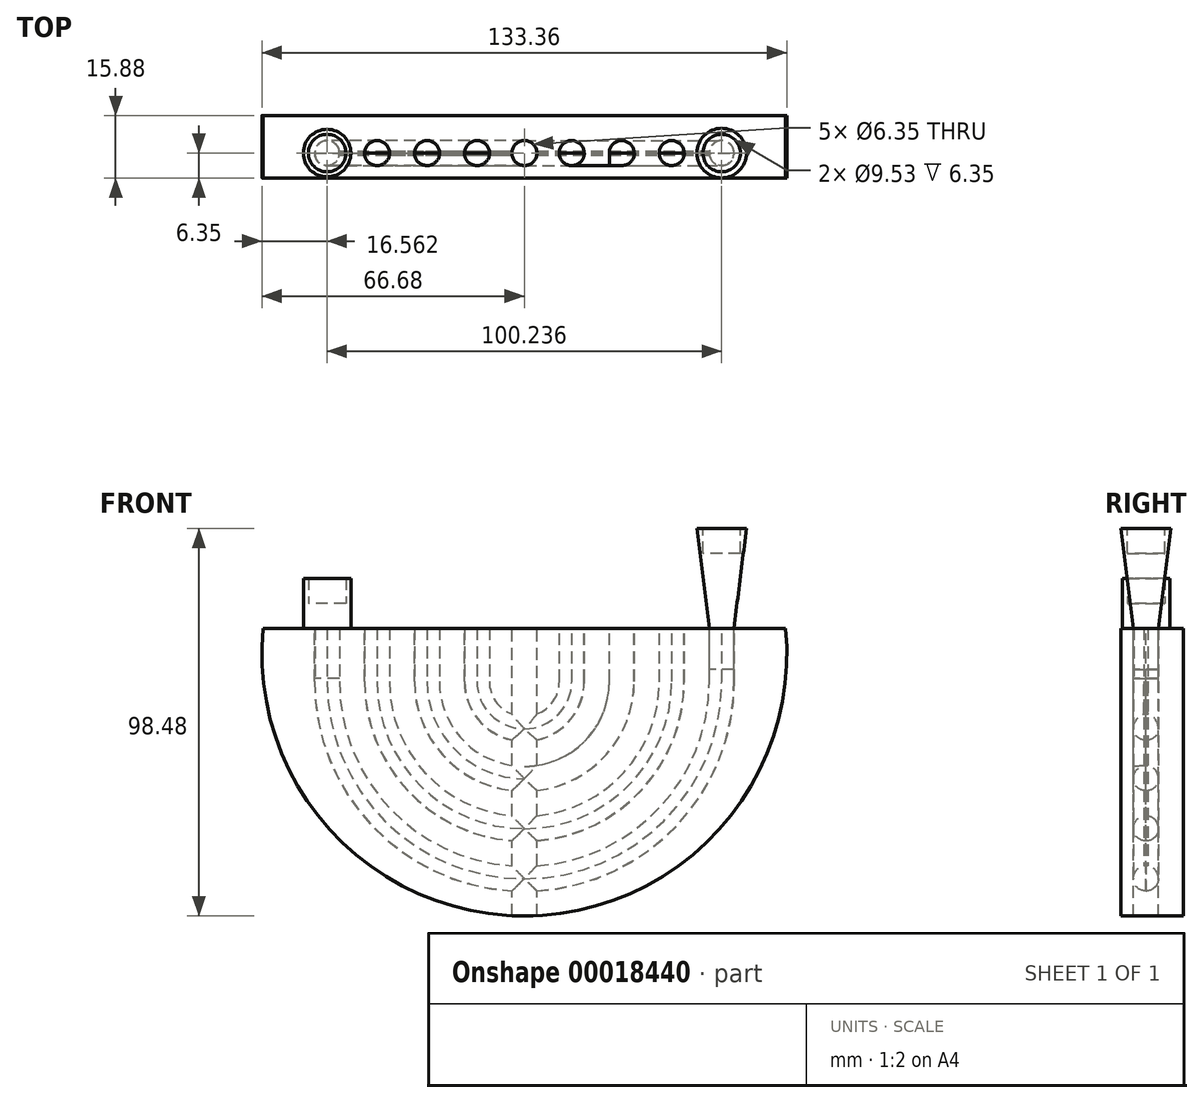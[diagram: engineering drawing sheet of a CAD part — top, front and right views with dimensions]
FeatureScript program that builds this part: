
annotation { "Feature Type Name" : "Feature", "Feature Type Description" : "" }
export const myFeature = defineFeature(function(context is Context, id is Id, definition is map)
    precondition{}
    {
        {
            var Q0;
            Q0=qCreatedBy(makeId("Front.planeOp"),FACE);
            var sketch = newSketch(context, id + "F0", { "sketchPlane" : qUnion([Q0])});
            skArc(sketch, "E0", {"start": v(-66.37, 6.4) * mm, "mid": v(0, -66.68) * mm, "end": v(66.37, 6.4) * mm});
            skLineSegment(sketch, "E1", {"start": v(-66.37, 6.4) * mm, "end": v(66.37, 6.4) * mm});
            skSolve(sketch);
        }
        {
            var Q0;
            Q0=qSketchRegion(id+"F0",true);
            extrude(context, id + "F1", {"entities" : qUnion([Q0]), "depth" : 12.7 * mm});
        }
        {
            var Q0;
            Q0=qCreatedBy(makeId("Front.planeOp"),FACE);
            var sketch = newSketch(context, id + "F2", { "sketchPlane" : qUnion([Q0])});
            skLineSegment(sketch, "E2.left", {"start": v(-3.18, 6.4) * mm, "end": v(-3.18, -15.38) * mm});
            skLineSegment(sketch, "E2.right", {"start": v(3.18, 6.4) * mm, "end": v(3.18, -15.38) * mm});
            skArc(sketch, "E3", {"start": v(-53.34, -7.07) * mm, "mid": v(-38.82, -43.65) * mm, "end": v(-3.18, -60.32) * mm});
            skArc(sketch, "E4.0", {"start": v(-46.99, -7.07) * mm, "mid": v(-34.33, -39.16) * mm, "end": v(-3.18, -53.96) * mm});
            skArc(sketch, "E5.0", {"start": v(-40.64, -7.07) * mm, "mid": v(-29.84, -34.67) * mm, "end": v(-3.18, -47.59) * mm});
            skArc(sketch, "E6.0", {"start": v(-34.29, -7.07) * mm, "mid": v(-25.34, -30.17) * mm, "end": v(-3.18, -41.22) * mm});
            skArc(sketch, "E7.0", {"start": v(-27.94, -7.07) * mm, "mid": v(-20.85, -25.67) * mm, "end": v(-3.18, -34.83) * mm});
            skArc(sketch, "E8.0", {"start": v(-21.59, -7.07) * mm, "mid": v(-16.35, -21.17) * mm, "end": v(-3.18, -28.43) * mm});
            skArc(sketch, "E9.0", {"start": v(-15.24, -7.07) * mm, "mid": v(-11.85, -16.66) * mm, "end": v(-3.18, -21.98) * mm});
            skArc(sketch, "E10.0", {"start": v(-8.9, -7.07) * mm, "mid": v(-7.32, -12.11) * mm, "end": v(-3.18, -15.38) * mm});
            skLineSegment(sketch, "E11", {"start": v(8.9, -7.07) * mm, "end": v(8.9, 6.4) * mm});
            skLineSegment(sketch, "E12", {"start": v(15.24, -7.07) * mm, "end": v(15.24, 8.22) * mm});
            skLineSegment(sketch, "E13", {"start": v(21.59, -7.07) * mm, "end": v(21.59, 6.4) * mm});
            skLineSegment(sketch, "E14", {"start": v(27.94, -7.07) * mm, "end": v(27.94, 6.4) * mm});
            skLineSegment(sketch, "E15", {"start": v(34.29, -7.07) * mm, "end": v(34.29, 6.4) * mm});
            skLineSegment(sketch, "E16", {"start": v(40.64, -7.07) * mm, "end": v(40.64, 6.4) * mm});
            skLineSegment(sketch, "E17", {"start": v(46.99, -7.07) * mm, "end": v(46.99, 6.4) * mm});
            skLineSegment(sketch, "E18", {"start": v(53.34, -7.07) * mm, "end": v(53.34, 6.4) * mm});
            skLineSegment(sketch, "E19", {"start": v(53.34, 6.4) * mm, "end": v(46.99, 6.4) * mm});
            skLineSegment(sketch, "E20", {"start": v(-15.24, -7.07) * mm, "end": v(-15.24, 6.4) * mm});
            skLineSegment(sketch, "E21", {"start": v(-8.9, -7.07) * mm, "end": v(-8.9, 6.4) * mm});
            skLineSegment(sketch, "E22", {"start": v(-21.59, -7.07) * mm, "end": v(-21.59, 6.4) * mm});
            skLineSegment(sketch, "E23", {"start": v(-27.94, -7.07) * mm, "end": v(-27.94, 6.4) * mm});
            skLineSegment(sketch, "E24", {"start": v(-34.29, -7.07) * mm, "end": v(-34.29, 6.4) * mm});
            skLineSegment(sketch, "E25", {"start": v(-40.64, -7.07) * mm, "end": v(-40.64, 6.4) * mm});
            skLineSegment(sketch, "E26", {"start": v(-46.99, -7.07) * mm, "end": v(-46.99, 6.4) * mm});
            skLineSegment(sketch, "E27", {"start": v(-53.34, -7.07) * mm, "end": v(-53.34, 6.4) * mm});
            skLineSegment(sketch, "E28.trimOffspring", {"start": v(40.64, 6.4) * mm, "end": v(34.29, 6.4) * mm});
            skLineSegment(sketch, "E29.trimOffspring", {"start": v(27.94, 6.4) * mm, "end": v(21.59, 6.4) * mm});
            skLineSegment(sketch, "E30.trimOffspring", {"start": v(15.24, 6.4) * mm, "end": v(8.9, 6.4) * mm});
            skLineSegment(sketch, "E31.trimOffspring", {"start": v(-21.59, 6.4) * mm, "end": v(-27.94, 6.4) * mm});
            skLineSegment(sketch, "E32.trimOffspring", {"start": v(-34.29, 6.4) * mm, "end": v(-40.64, 6.4) * mm});
            skLineSegment(sketch, "E33.trimOffspring", {"start": v(-46.99, 6.4) * mm, "end": v(-53.34, 6.4) * mm});
            skLineSegment(sketch, "E34", {"start": v(-15.24, 6.4) * mm, "end": v(-8.9, 6.4) * mm});
            skLineSegment(sketch, "E35.trimOffspring", {"start": v(-3.18, 6.4) * mm, "end": v(3.18, 6.4) * mm});
            skArc(sketch, "E36.trimOffspring", {"start": v(3.18, -15.38) * mm, "mid": v(7.32, -12.11) * mm, "end": v(8.9, -7.07) * mm});
            skLineSegment(sketch, "E37.trimOffspring", {"start": v(3.18, -21.98) * mm, "end": v(3.18, -28.43) * mm});
            skLineSegment(sketch, "E38.trimOffspring", {"start": v(-3.18, -21.98) * mm, "end": v(-3.18, -28.43) * mm});
            skLineSegment(sketch, "E39.trimOffspring", {"start": v(-3.18, -34.83) * mm, "end": v(-3.18, -41.22) * mm});
            skArc(sketch, "E40.trimOffspring", {"start": v(3.18, -28.43) * mm, "mid": v(16.35, -21.17) * mm, "end": v(21.59, -7.07) * mm});
            skArc(sketch, "E41.trimOffspring", {"start": v(3.18, -21.98) * mm, "mid": v(11.85, -16.66) * mm, "end": v(15.24, -7.07) * mm});
            skLineSegment(sketch, "E42.trimOffspring", {"start": v(3.18, -34.83) * mm, "end": v(3.18, -41.22) * mm});
            skArc(sketch, "E43.trimOffspring", {"start": v(3.17, -34.83) * mm, "mid": v(20.85, -25.67) * mm, "end": v(27.94, -7.07) * mm});
            skArc(sketch, "E44.trimOffspring", {"start": v(3.18, -41.22) * mm, "mid": v(25.34, -30.17) * mm, "end": v(34.29, -7.07) * mm});
            skLineSegment(sketch, "E45.trimOffspring", {"start": v(3.18, -47.59) * mm, "end": v(3.18, -53.96) * mm});
            skLineSegment(sketch, "E46.trimOffspring", {"start": v(-3.18, -47.59) * mm, "end": v(-3.18, -53.96) * mm});
            skArc(sketch, "E47.trimOffspring", {"start": v(3.18, -47.59) * mm, "mid": v(29.84, -34.67) * mm, "end": v(40.64, -7.07) * mm});
            skLineSegment(sketch, "E48.trimOffspring", {"start": v(3.18, -60.32) * mm, "end": v(3.18, -66.6) * mm});
            skLineSegment(sketch, "E49.trimOffspring", {"start": v(-3.18, -60.32) * mm, "end": v(-3.18, -66.6) * mm});
            skArc(sketch, "E50.trimOffspring", {"start": v(3.17, -53.96) * mm, "mid": v(34.33, -39.16) * mm, "end": v(46.99, -7.07) * mm});
            skArc(sketch, "E51.trimOffspring", {"start": v(3.17, -60.32) * mm, "mid": v(38.82, -43.65) * mm, "end": v(53.34, -7.07) * mm});
            skArc(sketch, "E52.0", {"start": v(-3.17, -66.6) * mm, "mid": v(0, -66.68) * mm, "end": v(3.18, -66.6) * mm});
            skPoint(sketch, "E53.orphan", {"position": v(-66.37, 6.4) * mm});
            skPoint(sketch, "E54.orphan", {"position": v(66.37, 6.4) * mm});
            skSolve(sketch);
        }
        {
            var Q0;
            Q0=qSketchRegion(id+"F2",true);
            var Q1;
            Q1=makeQuery(id+"F1.opExtrude","CAP_FACE",FACE,{"disambiguationData":[OSD([sQuery(id+"F0.wireOp",EDGE,"E0")])],"isStart":false});
            extrude(context, id + "F3", {"entities" : qUnion([Q0]), "operationType" : NewBodyOperationType.REMOVE, "endBoundEntityFace" : qUnion([Q1]), "depth" : 9.52 * mm});
        }
        {
            var Q0;
            Q0=qCreatedBy(makeId("Front.planeOp"),FACE);
            cPlane(context, id + "F4", {"entities" : qUnion([Q0]), "cplaneType" : CPlaneType.OFFSET, "offset" : 6.35 * mm, "width" : 152.4 * mm, "height" : 152.4 * mm});
        }
        {
            var Q0;
            Q0=makeQuery(id+"F1.opExtrude","SWEPT_FACE",FACE,{"disambiguationData":[OSD([sQuery(id+"F0.wireOp",EDGE,"E1")])]});
            var sketch = newSketch(context, id + "F5", { "sketchPlane" : qUnion([Q0])});
            skPoint(sketch, "E55.0", {"position": v(-50.12, -6.35) * mm});
            skPoint(sketch, "E56.0", {"position": v(-37.42, -6.35) * mm});
            skPoint(sketch, "E57.0", {"position": v(-24.72, -6.35) * mm});
            skPoint(sketch, "E58.0", {"position": v(-12.02, -6.35) * mm});
            skPoint(sketch, "E59.0", {"position": v(0, -6.35) * mm});
            skPoint(sketch, "E60.0", {"position": v(12.02, -6.35) * mm});
            skPoint(sketch, "E61.0", {"position": v(24.72, -6.35) * mm});
            skPoint(sketch, "E62.0", {"position": v(37.42, -6.35) * mm});
            skPoint(sketch, "E63.0", {"position": v(50.12, -6.35) * mm});
            skCircle(sketch, "E64", {"center": v(-37.42, -6.35) * mm, "radius": 3.18 * mm});
            skCircle(sketch, "E65", {"center": v(-24.72, -6.35) * mm, "radius": 3.18 * mm});
            skCircle(sketch, "E66", {"center": v(-12.02, -6.35) * mm, "radius": 3.18 * mm});
            skCircle(sketch, "E67", {"center": v(0, -6.35) * mm, "radius": 3.18 * mm});
            skCircle(sketch, "E68", {"center": v(12.02, -6.35) * mm, "radius": 3.18 * mm});
            skCircle(sketch, "E69", {"center": v(24.72, -6.35) * mm, "radius": 3.18 * mm});
            skCircle(sketch, "E70", {"center": v(37.42, -6.35) * mm, "radius": 3.18 * mm});
            skCircle(sketch, "E71", {"center": v(50.12, -6.35) * mm, "radius": 3.18 * mm});
            skCircle(sketch, "E72", {"center": v(-50.12, -6.35) * mm, "radius": 3.18 * mm});
            skSolve(sketch);
        }
        {
            var Q0;
            Q0=qSketchRegion(id+"F5",true);
            extrude(context, id + "F6", {"entities" : qUnion([Q0]), "operationType" : NewBodyOperationType.REMOVE, "endBound" : BoundingType.THROUGH_ALL, "depth" : 25.4 * mm});
        }
        {
            var Q0;
            Q0=makeQuery(id+"F3.boolean.opBoolean","COPY",EDGE,{"derivedFrom":makeQuery(id+"F3.opExtrude","CAP_EDGE",EDGE,{"disambiguationData":[OSD([sQuery(id+"F2.wireOp",EDGE,"E51.trimOffspring")])],"isStart":false})});
            var Q1;
            Q1=makeQuery(id+"F3.boolean.opBoolean","COPY",EDGE,{"derivedFrom":makeQuery(id+"F3.opExtrude","CAP_EDGE",EDGE,{"disambiguationData":[OSD([sQuery(id+"F2.wireOp",EDGE,"E50.trimOffspring")])],"isStart":false})});
            var Q2;
            Q2=makeQuery(id+"F3.boolean.opBoolean","COPY",EDGE,{"derivedFrom":makeQuery(id+"F3.opExtrude","CAP_EDGE",EDGE,{"disambiguationData":[OSD([sQuery(id+"F2.wireOp",EDGE,"E47.trimOffspring")])],"isStart":false})});
            var Q3;
            Q3=makeQuery(id+"F3.boolean.opBoolean","COPY",EDGE,{"derivedFrom":makeQuery(id+"F3.opExtrude","CAP_EDGE",EDGE,{"disambiguationData":[OSD([sQuery(id+"F2.wireOp",EDGE,"E44.trimOffspring")])],"isStart":false})});
            var Q4;
            Q4=makeQuery(id+"F3.boolean.opBoolean","COPY",EDGE,{"derivedFrom":makeQuery(id+"F3.opExtrude","CAP_EDGE",EDGE,{"disambiguationData":[OSD([sQuery(id+"F2.wireOp",EDGE,"E43.trimOffspring")])],"isStart":false})});
            var Q5;
            Q5=makeQuery(id+"F3.boolean.opBoolean","COPY",EDGE,{"derivedFrom":makeQuery(id+"F3.opExtrude","CAP_EDGE",EDGE,{"disambiguationData":[OSD([sQuery(id+"F2.wireOp",EDGE,"E40.trimOffspring")])],"isStart":false})});
            var Q6;
            Q6=makeQuery(id+"F3.boolean.opBoolean","COPY",EDGE,{"derivedFrom":makeQuery(id+"F3.opExtrude","CAP_EDGE",EDGE,{"disambiguationData":[OSD([sQuery(id+"F2.wireOp",EDGE,"E41.trimOffspring")])],"isStart":false})});
            var Q7;
            Q7=makeQuery(id+"F3.boolean.opBoolean","COPY",EDGE,{"derivedFrom":makeQuery(id+"F3.opExtrude","CAP_EDGE",EDGE,{"disambiguationData":[OSD([sQuery(id+"F2.wireOp",EDGE,"E36.trimOffspring")])],"isStart":false})});
            var Q8;
            Q8=makeQuery(id+"F3.boolean.opBoolean","COPY",EDGE,{"derivedFrom":makeQuery(id+"F3.opExtrude","CAP_EDGE",EDGE,{"disambiguationData":[OSD([sQuery(id+"F2.wireOp",EDGE,"E2.right")])],"isStart":false})});
            var Q9;
            Q9=makeQuery(id+"F3.boolean.opBoolean","COPY",EDGE,{"derivedFrom":makeQuery(id+"F3.opExtrude","CAP_EDGE",EDGE,{"disambiguationData":[OSD([sQuery(id+"F2.wireOp",EDGE,"E37.trimOffspring")])],"isStart":false})});
            var Q10;
            Q10=makeQuery(id+"F3.boolean.opBoolean","COPY",EDGE,{"derivedFrom":makeQuery(id+"F3.opExtrude","CAP_EDGE",EDGE,{"disambiguationData":[OSD([sQuery(id+"F2.wireOp",EDGE,"E42.trimOffspring")])],"isStart":false})});
            var Q11;
            Q11=makeQuery(id+"F3.boolean.opBoolean","COPY",EDGE,{"derivedFrom":makeQuery(id+"F3.opExtrude","CAP_EDGE",EDGE,{"disambiguationData":[OSD([sQuery(id+"F2.wireOp",EDGE,"E45.trimOffspring")])],"isStart":false})});
            var Q12;
            Q12=makeQuery(id+"F3.boolean.opBoolean","COPY",EDGE,{"derivedFrom":makeQuery(id+"F3.opExtrude","CAP_EDGE",EDGE,{"disambiguationData":[OSD([sQuery(id+"F2.wireOp",EDGE,"E48.trimOffspring")])],"isStart":false})});
            var Q13;
            Q13=makeQuery(id+"F3.boolean.opBoolean","COPY",EDGE,{"derivedFrom":makeQuery(id+"F3.opExtrude","CAP_EDGE",EDGE,{"disambiguationData":[OSD([sQuery(id+"F2.wireOp",EDGE,"E49.trimOffspring")])],"isStart":false})});
            var Q14;
            Q14=makeQuery(id+"F3.boolean.opBoolean","COPY",EDGE,{"derivedFrom":makeQuery(id+"F3.opExtrude","CAP_EDGE",EDGE,{"disambiguationData":[OSD([sQuery(id+"F2.wireOp",EDGE,"E46.trimOffspring")])],"isStart":false})});
            var Q15;
            Q15=makeQuery(id+"F3.boolean.opBoolean","COPY",EDGE,{"derivedFrom":makeQuery(id+"F3.opExtrude","CAP_EDGE",EDGE,{"disambiguationData":[OSD([sQuery(id+"F2.wireOp",EDGE,"E39.trimOffspring")])],"isStart":false})});
            var Q16;
            Q16=makeQuery(id+"F3.boolean.opBoolean","COPY",EDGE,{"derivedFrom":makeQuery(id+"F3.opExtrude","CAP_EDGE",EDGE,{"disambiguationData":[OSD([sQuery(id+"F2.wireOp",EDGE,"E38.trimOffspring")])],"isStart":false})});
            var Q17;
            Q17=makeQuery(id+"F3.boolean.opBoolean","COPY",EDGE,{"derivedFrom":makeQuery(id+"F3.opExtrude","CAP_EDGE",EDGE,{"disambiguationData":[OSD([sQuery(id+"F2.wireOp",EDGE,"E2.left")])],"isStart":false})});
            var Q18;
            Q18=makeQuery(id+"F3.boolean.opBoolean","COPY",EDGE,{"derivedFrom":makeQuery(id+"F3.opExtrude","CAP_EDGE",EDGE,{"disambiguationData":[OSD([sQuery(id+"F2.wireOp",EDGE,"E10.0")])],"isStart":false})});
            var Q19;
            Q19=makeQuery(id+"F3.boolean.opBoolean","COPY",EDGE,{"derivedFrom":makeQuery(id+"F3.opExtrude","CAP_EDGE",EDGE,{"disambiguationData":[OSD([sQuery(id+"F2.wireOp",EDGE,"E9.0")])],"isStart":false})});
            var Q20;
            Q20=makeQuery(id+"F3.boolean.opBoolean","COPY",EDGE,{"derivedFrom":makeQuery(id+"F3.opExtrude","CAP_EDGE",EDGE,{"disambiguationData":[OSD([sQuery(id+"F2.wireOp",EDGE,"E7.0")])],"isStart":false})});
            var Q21;
            Q21=makeQuery(id+"F3.boolean.opBoolean","COPY",EDGE,{"derivedFrom":makeQuery(id+"F3.opExtrude","CAP_EDGE",EDGE,{"disambiguationData":[OSD([sQuery(id+"F2.wireOp",EDGE,"E5.0")])],"isStart":false})});
            var Q22;
            Q22=makeQuery(id+"F3.boolean.opBoolean","COPY",EDGE,{"derivedFrom":makeQuery(id+"F3.opExtrude","CAP_EDGE",EDGE,{"disambiguationData":[OSD([sQuery(id+"F2.wireOp",EDGE,"E3")])],"isStart":false})});
            var Q23;
            Q23=makeQuery(id+"F3.boolean.opBoolean","COPY",EDGE,{"derivedFrom":makeQuery(id+"F3.opExtrude","CAP_EDGE",EDGE,{"disambiguationData":[OSD([sQuery(id+"F2.wireOp",EDGE,"E4.0")])],"isStart":false})});
            var Q24;
            Q24=makeQuery(id+"F3.boolean.opBoolean","COPY",EDGE,{"derivedFrom":makeQuery(id+"F3.opExtrude","CAP_EDGE",EDGE,{"disambiguationData":[OSD([sQuery(id+"F2.wireOp",EDGE,"E6.0")])],"isStart":false})});
            var Q25;
            Q25=makeQuery(id+"F3.boolean.opBoolean","COPY",EDGE,{"derivedFrom":makeQuery(id+"F3.opExtrude","CAP_EDGE",EDGE,{"disambiguationData":[OSD([sQuery(id+"F2.wireOp",EDGE,"171504de-b975-4acb-bd22-756de7e579bb.0")])],"isStart":false})});
            var Q26;
            Q26=makeQuery(id+"F3.boolean.opBoolean","COPY",EDGE,{"derivedFrom":makeQuery(id+"F3.opExtrude","CAP_EDGE",EDGE,{"disambiguationData":[OSD([sQuery(id+"F2.wireOp",EDGE,"E22")])],"isStart":false})});
            var Q27;
            Q27=makeQuery(id+"F3.boolean.opBoolean","COPY",EDGE,{"derivedFrom":makeQuery(id+"F3.opExtrude","CAP_EDGE",EDGE,{"disambiguationData":[OSD([sQuery(id+"F2.wireOp",EDGE,"E8.0")])],"isStart":false})});
            fillet(context, id + "F7", {"entities" : qUnion([Q0, Q1, Q2, Q3, Q4, Q5, Q6, Q7, Q8, Q9, Q10, Q11, Q12, Q13, Q14, Q15, Q16, Q17, Q18, Q19, Q20, Q21, Q22, Q23, Q24, Q25, Q26, Q27]), "radius" : 3.17 * mm, "tangentPropagation" : true, "allowEdgeOverflow" : false});
        }
        {
            var Q0;
            Q0=qSketchRegion(id+"F2",true);
            extrude(context, id + "F8", {"entities" : qUnion([Q0]), "depth" : 6.35 * mm});
        }
        {
            var Q0;
            Q0=makeQuery(id+"F8.opExtrude","SWEPT_FACE",FACE,{"disambiguationData":[OSD([sQuery(id+"F2.wireOp",EDGE,"E30.trimOffspring")])]});
            cPlane(context, id + "F9", {"entities" : qUnion([Q0]), "cplaneType" : CPlaneType.OFFSET, "offset" : 0 * mm, "width" : 152.4 * mm, "height" : 152.4 * mm});
        }
        {
            var Q0;
            Q0=qCreatedBy(id+"F9.planeOp",FACE);
            var sketch = newSketch(context, id + "F10", { "sketchPlane" : qUnion([Q0])});
            skArc(sketch, "E73", {"start": v(-46.99, -6.35) * mm, "mid": v(-50.16, -3.17) * mm, "end": v(-53.34, -6.35) * mm});
            skArc(sketch, "E74", {"start": v(-34.29, -6.35) * mm, "mid": v(-37.47, -3.17) * mm, "end": v(-40.64, -6.35) * mm});
            skArc(sketch, "E75", {"start": v(-21.59, -6.35) * mm, "mid": v(-24.76, -3.18) * mm, "end": v(-27.94, -6.35) * mm});
            skArc(sketch, "E76", {"start": v(-8.9, -6.35) * mm, "mid": v(-12.07, -3.18) * mm, "end": v(-15.24, -6.35) * mm});
            skArc(sketch, "E77", {"start": v(3.18, -6.35) * mm, "mid": v(0, -3.18) * mm, "end": v(-3.17, -6.35) * mm});
            skArc(sketch, "E78", {"start": v(15.24, -6.35) * mm, "mid": v(12.07, -3.18) * mm, "end": v(8.9, -6.35) * mm});
            skArc(sketch, "E79", {"start": v(27.94, -6.35) * mm, "mid": v(24.76, -3.18) * mm, "end": v(21.59, -6.35) * mm});
            skArc(sketch, "E80", {"start": v(40.64, -6.35) * mm, "mid": v(37.47, -3.18) * mm, "end": v(34.3, -6.35) * mm});
            skArc(sketch, "E81", {"start": v(53.34, -6.35) * mm, "mid": v(50.16, -3.18) * mm, "end": v(46.99, -6.35) * mm});
            skSolve(sketch);
        }
        {
            var Q0;
            Q0=makeQuery(id+"F8.opExtrude","SWEPT_FACE",FACE,{"disambiguationData":[OSD([sQuery(id+"F2.wireOp",EDGE,"E33.trimOffspring")])]});
            var sketch = newSketch(context, id + "F11", { "sketchPlane" : qUnion([Q0])});
            skArc(sketch, "E82.0", {"start": v(-46.99, -6.35) * mm, "mid": v(-50.16, -3.17) * mm, "end": v(-53.34, -6.35) * mm});
            skSolve(sketch);
        }
        {
            var Q0;
            Q0=makeQuery(id+"F8.opExtrude","SWEPT_FACE",FACE,{"disambiguationData":[OSD([sQuery(id+"F2.wireOp",EDGE,"E32.trimOffspring")])]});
            var sketch = newSketch(context, id + "F12", { "sketchPlane" : qUnion([Q0])});
            skArc(sketch, "E83.0", {"start": v(-34.29, -6.35) * mm, "mid": v(-37.47, -3.17) * mm, "end": v(-40.64, -6.35) * mm});
            skSolve(sketch);
        }
        {
            var Q0;
            Q0=makeQuery(id+"F8.opExtrude","SWEPT_FACE",FACE,{"disambiguationData":[OSD([sQuery(id+"F2.wireOp",EDGE,"E31.trimOffspring")])]});
            var sketch = newSketch(context, id + "F13", { "sketchPlane" : qUnion([Q0])});
            skArc(sketch, "E84.0", {"start": v(-21.59, -6.35) * mm, "mid": v(-24.76, -3.18) * mm, "end": v(-27.94, -6.35) * mm});
            skSolve(sketch);
        }
        {
            var Q0;
            Q0=makeQuery(id+"F8.opExtrude","SWEPT_FACE",FACE,{"disambiguationData":[OSD([sQuery(id+"F2.wireOp",EDGE,"E34")])]});
            var sketch = newSketch(context, id + "F14", { "sketchPlane" : qUnion([Q0])});
            skArc(sketch, "E85.0", {"start": v(-8.9, -6.35) * mm, "mid": v(-12.07, -3.18) * mm, "end": v(-15.24, -6.35) * mm});
            skSolve(sketch);
        }
        {
            var Q0;
            Q0=makeQuery(id+"F1.opExtrude","SWEPT_FACE",FACE,{"disambiguationData":[OSD([sQuery(id+"F0.wireOp",EDGE,"E1")])]});
            var sketch = newSketch(context, id + "F15", { "sketchPlane" : qUnion([Q0])});
            skArc(sketch, "E86.0", {"start": v(3.18, -6.35) * mm, "mid": v(0, -3.18) * mm, "end": v(-3.17, -6.35) * mm});
            skLineSegment(sketch, "E87.0", {"start": v(-3.18, -6.35) * mm, "end": v(-3.18, 0) * mm});
            skLineSegment(sketch, "E88.0", {"start": v(-3.17, 0) * mm, "end": v(3.17, 0) * mm});
            skLineSegment(sketch, "E89.0", {"start": v(3.18, -6.35) * mm, "end": v(3.18, 0) * mm});
            skArc(sketch, "E90.0", {"start": v(15.24, -6.35) * mm, "mid": v(12.07, -3.18) * mm, "end": v(8.9, -6.35) * mm});
            skLineSegment(sketch, "E91.0", {"start": v(8.9, -6.35) * mm, "end": v(8.9, 0) * mm});
            skLineSegment(sketch, "E92.0", {"start": v(15.24, 0) * mm, "end": v(8.9, 0) * mm});
            skLineSegment(sketch, "E93.0", {"start": v(15.24, -6.35) * mm, "end": v(15.24, 0) * mm});
            skLineSegment(sketch, "E94.0", {"start": v(21.59, -6.35) * mm, "end": v(21.59, 0) * mm});
            skLineSegment(sketch, "E95.0", {"start": v(27.94, 0) * mm, "end": v(21.59, 0) * mm});
            skLineSegment(sketch, "E96.0", {"start": v(27.94, -6.35) * mm, "end": v(27.94, 0) * mm});
            skArc(sketch, "E97.0", {"start": v(27.94, -6.35) * mm, "mid": v(24.76, -3.18) * mm, "end": v(21.59, -6.35) * mm});
            skArc(sketch, "E98.0", {"start": v(40.64, -6.35) * mm, "mid": v(37.47, -3.18) * mm, "end": v(34.3, -6.35) * mm});
            skLineSegment(sketch, "E99.0", {"start": v(34.29, -6.35) * mm, "end": v(34.29, 0) * mm});
            skLineSegment(sketch, "E100.0", {"start": v(40.64, 0) * mm, "end": v(34.29, 0) * mm});
            skLineSegment(sketch, "E101.0", {"start": v(40.64, -6.35) * mm, "end": v(40.64, 0) * mm});
            skLineSegment(sketch, "E102.0", {"start": v(46.99, -6.35) * mm, "end": v(46.99, 0) * mm});
            skArc(sketch, "E103.0", {"start": v(53.34, -6.35) * mm, "mid": v(50.16, -3.18) * mm, "end": v(46.99, -6.35) * mm});
            skLineSegment(sketch, "E104.0", {"start": v(53.34, -6.35) * mm, "end": v(53.34, 0) * mm});
            skLineSegment(sketch, "E105.0", {"start": v(53.34, 0) * mm, "end": v(46.99, 0) * mm});
            skLineSegment(sketch, "E106.0", {"start": v(-15.24, -6.35) * mm, "end": v(-15.24, 0) * mm});
            skArc(sketch, "E107.0", {"start": v(-8.9, -6.35) * mm, "mid": v(-12.07, -3.18) * mm, "end": v(-15.24, -6.35) * mm});
            skLineSegment(sketch, "E108.0", {"start": v(-15.24, 0) * mm, "end": v(-8.9, 0) * mm});
            skLineSegment(sketch, "E109.0", {"start": v(-8.9, -6.35) * mm, "end": v(-8.9, 0) * mm});
            skArc(sketch, "E110.0", {"start": v(-21.59, -6.35) * mm, "mid": v(-24.76, -3.18) * mm, "end": v(-27.94, -6.35) * mm});
            skLineSegment(sketch, "E111.0", {"start": v(-27.94, -6.35) * mm, "end": v(-27.94, 0) * mm});
            skLineSegment(sketch, "E112.0", {"start": v(-21.59, 0) * mm, "end": v(-27.94, 0) * mm});
            skLineSegment(sketch, "E113.0", {"start": v(-21.59, -6.35) * mm, "end": v(-21.59, 0) * mm});
            skArc(sketch, "E114.0", {"start": v(-34.29, -6.35) * mm, "mid": v(-37.47, -3.17) * mm, "end": v(-40.64, -6.35) * mm});
            skLineSegment(sketch, "E115.0", {"start": v(-34.29, 0) * mm, "end": v(-40.64, 0) * mm});
            skLineSegment(sketch, "E116.0", {"start": v(-34.29, -6.35) * mm, "end": v(-34.29, 0) * mm});
            skArc(sketch, "E117.0", {"start": v(-46.99, -6.35) * mm, "mid": v(-50.16, -3.17) * mm, "end": v(-53.34, -6.35) * mm});
            skLineSegment(sketch, "E118.0", {"start": v(-53.34, -6.35) * mm, "end": v(-53.34, 0) * mm});
            skLineSegment(sketch, "E119.0", {"start": v(-46.99, 0) * mm, "end": v(-53.34, 0) * mm});
            skLineSegment(sketch, "E120.0", {"start": v(-46.99, -6.35) * mm, "end": v(-46.99, 0) * mm});
            skLineSegment(sketch, "E121.0", {"start": v(-40.64, -6.35) * mm, "end": v(-40.64, 0) * mm});
            skSolve(sketch);
        }
        {
            var Q0;
            Q0=makeQuery(id+"F15.imprint","IMPRINT",FACE,{"disambiguationData":[TD([[makeQuery(id+"F15.imprint","IMPRINT",EDGE,{"derivedFrom":sQuery(id+"F15.wireOp",EDGE,"E86.0")}),-1.0]])]});
            var Q1;
            Q1=makeQuery(id+"F8.opExtrude","SWEPT_FACE",FACE,{"disambiguationData":[OSD([sQuery(id+"F2.wireOp",EDGE,"E52.0")])]});
            extrude(context, id + "F16", {"entities" : qUnion([Q0]), "endBound" : BoundingType.UP_TO_SURFACE, "oppositeDirection" : true, "endBoundEntityFace" : qUnion([Q1]), "depth" : 25.4 * mm});
        }
        {
            var Q0;
            Q0=makeQuery(id+"F12.imprint","IMPRINT",FACE,{"disambiguationData":[TD([[makeQuery(id+"F12.imprint","IMPRINT",EDGE,{"derivedFrom":sQuery(id+"F12.wireOp",EDGE,"E83.0")}),-1.0]])]});
            var Q1;
            Q1=makeQuery(id+"F8.opExtrude","CAP_EDGE",EDGE,{"disambiguationData":[OSD([sQuery(id+"F2.wireOp",EDGE,"E24")])],"isStart":false});
            var Q2;
            Q2=makeQuery(id+"F8.opExtrude","CAP_EDGE",EDGE,{"disambiguationData":[OSD([sQuery(id+"F2.wireOp",EDGE,"E6.0")])],"isStart":false});
            sweep(context, id + "F17", {"profiles" : qUnion([Q0]), "path" : qUnion([Q1, Q2])});
        }
        {
            var Q0;
            Q0=qSketchRegion(id+"F2",true);
            extrude(context, id + "F18", {"entities" : qUnion([Q0]), "depth" : 6.35 * mm});
        }
        {
            var Q0;
            Q0=makeQuery(id+"F18.opExtrude","SWEPT_FACE",FACE,{"disambiguationData":[OSD([sQuery(id+"F2.wireOp",EDGE,"E35.trimOffspring")])]});
            var sketch = newSketch(context, id + "F19", { "sketchPlane" : qUnion([Q0])});
            skArc(sketch, "E122.0", {"start": v(3.18, -6.35) * mm, "mid": v(0, -3.18) * mm, "end": v(-3.17, -6.35) * mm});
            skSolve(sketch);
        }
        {
            var Q0;
            Q0=makeQuery(id+"F19.imprint","IMPRINT",FACE,{"disambiguationData":[TD([[makeQuery(id+"F19.imprint","IMPRINT",EDGE,{"derivedFrom":sQuery(id+"F19.wireOp",EDGE,"E122.0")}),1.0]])]});
            extrude(context, id + "F20", {"entities" : qUnion([Q0]), "operationType" : NewBodyOperationType.REMOVE, "endBound" : BoundingType.THROUGH_ALL, "oppositeDirection" : true, "depth" : 25.4 * mm});
        }
        {
            var Q0;
            Q0=makeQuery(id+"F17.opSweep","SWEPT_BODY",BODY,{"disambiguationData":[OSD([sQuery(id+"F2.wireOp",EDGE,"E6.0"),sQuery(id+"F2.wireOp",EDGE,"E24"),sQuery(id+"F2.wireOp",EDGE,"E25"),sQuery(id+"F2.wireOp",EDGE,"E32.trimOffspring"),sQuery(id+"F12.wireOp",EDGE,"E83.0")])]});
            deleteBodies(context, id + "F21", {"entities" : qUnion([Q0])});
        }
        {
            var Q0;
            Q0=makeQuery(id+"F16.opExtrude","SWEPT_BODY",BODY,{"disambiguationData":[OSD([sQuery(id+"F15.wireOp",EDGE,"E86.0"),sQuery(id+"F15.wireOp",EDGE,"E87.0"),sQuery(id+"F15.wireOp",EDGE,"E88.0"),sQuery(id+"F15.wireOp",EDGE,"E89.0")])]});
            deleteBodies(context, id + "F22", {"entities" : qUnion([Q0])});
        }
        {
            var Q0;
            Q0=makeQuery(id+"F8.opExtrude","SWEPT_BODY",BODY,{"disambiguationData":[OSD([sQuery(id+"F2.wireOp",EDGE,"E2.left"),sQuery(id+"F2.wireOp",EDGE,"E2.right"),sQuery(id+"F2.wireOp",EDGE,"E3"),sQuery(id+"F2.wireOp",EDGE,"E4.0"),sQuery(id+"F2.wireOp",EDGE,"E5.0"),sQuery(id+"F2.wireOp",EDGE,"E6.0"),sQuery(id+"F2.wireOp",EDGE,"E7.0"),sQuery(id+"F2.wireOp",EDGE,"E9.0"),sQuery(id+"F2.wireOp",EDGE,"171504de-b975-4acb-bd22-756de7e579bb.0"),sQuery(id+"F2.wireOp",EDGE,"E10.0"),sQuery(id+"F2.wireOp",EDGE,"E11"),sQuery(id+"F2.wireOp",EDGE,"E12"),sQuery(id+"F2.wireOp",EDGE,"E13"),sQuery(id+"F2.wireOp",EDGE,"E14"),sQuery(id+"F2.wireOp",EDGE,"E15"),sQuery(id+"F2.wireOp",EDGE,"E16"),sQuery(id+"F2.wireOp",EDGE,"E17"),sQuery(id+"F2.wireOp",EDGE,"E18"),sQuery(id+"F2.wireOp",EDGE,"E19"),sQuery(id+"F2.wireOp",EDGE,"E20"),sQuery(id+"F2.wireOp",EDGE,"E21"),sQuery(id+"F2.wireOp",EDGE,"E22"),sQuery(id+"F2.wireOp",EDGE,"E23"),sQuery(id+"F2.wireOp",EDGE,"E24"),sQuery(id+"F2.wireOp",EDGE,"E25"),sQuery(id+"F2.wireOp",EDGE,"E26"),sQuery(id+"F2.wireOp",EDGE,"E27"),sQuery(id+"F2.wireOp",EDGE,"E28.trimOffspring"),sQuery(id+"F2.wireOp",EDGE,"E29.trimOffspring"),sQuery(id+"F2.wireOp",EDGE,"E30.trimOffspring"),sQuery(id+"F2.wireOp",EDGE,"E31.trimOffspring"),sQuery(id+"F2.wireOp",EDGE,"E32.trimOffspring"),sQuery(id+"F2.wireOp",EDGE,"E33.trimOffspring"),sQuery(id+"F2.wireOp",EDGE,"E34"),sQuery(id+"F2.wireOp",EDGE,"E35.trimOffspring"),sQuery(id+"F2.wireOp",EDGE,"E36.trimOffspring"),sQuery(id+"F2.wireOp",EDGE,"E37.trimOffspring"),sQuery(id+"F2.wireOp",EDGE,"E38.trimOffspring"),sQuery(id+"F2.wireOp",EDGE,"E39.trimOffspring"),sQuery(id+"F2.wireOp",EDGE,"E41.trimOffspring"),sQuery(id+"F2.wireOp",EDGE,"E42.trimOffspring"),sQuery(id+"F2.wireOp",EDGE,"E40.trimOffspring"),sQuery(id+"F2.wireOp",EDGE,"E43.trimOffspring"),sQuery(id+"F2.wireOp",EDGE,"E44.trimOffspring"),sQuery(id+"F2.wireOp",EDGE,"E45.trimOffspring"),sQuery(id+"F2.wireOp",EDGE,"E46.trimOffspring"),sQuery(id+"F2.wireOp",EDGE,"E47.trimOffspring"),sQuery(id+"F2.wireOp",EDGE,"E48.trimOffspring"),sQuery(id+"F2.wireOp",EDGE,"E49.trimOffspring"),sQuery(id+"F2.wireOp",EDGE,"E50.trimOffspring"),sQuery(id+"F2.wireOp",EDGE,"E51.trimOffspring"),sQuery(id+"F2.wireOp",EDGE,"E52.0")])]});
            deleteBodies(context, id + "F23", {"entities" : qUnion([Q0])});
        }
        {
            var Q0;
            Q0=qCreatedBy(id+"F4.planeOp",FACE);
            var sketch = newSketch(context, id + "F24", { "sketchPlane" : qUnion([Q0])});
            skArc(sketch, "E123.0.0", {"start": v(-53.34, -7.07) * mm, "mid": v(-36.58, -45.9) * mm, "end": v(3.18, -60.32) * mm});
            skArc(sketch, "E123.0.2", {"start": v(-3.18, -53.96) * mm, "mid": v(-34.33, -39.16) * mm, "end": v(-46.99, -7.07) * mm});
            skLineSegment(sketch, "E123.0.3", {"start": v(-46.99, -7.07) * mm, "end": v(-46.99, 6.4) * mm});
            skLineSegment(sketch, "E123.0.4", {"start": v(-46.99, 6.4) * mm, "end": v(-53.34, 6.4) * mm});
            skLineSegment(sketch, "E123.0.5", {"start": v(-53.34, 6.4) * mm, "end": v(-53.34, -7.07) * mm});
            skArc(sketch, "E124.0.0", {"start": v(-40.64, -7.07) * mm, "mid": v(-29.84, -34.67) * mm, "end": v(-3.18, -47.59) * mm});
            skArc(sketch, "E124.0.2", {"start": v(3.18, -41.22) * mm, "mid": v(-23.1, -32.42) * mm, "end": v(-34.29, -7.07) * mm});
            skLineSegment(sketch, "E124.0.3", {"start": v(-34.29, -7.07) * mm, "end": v(-34.29, 6.4) * mm});
            skLineSegment(sketch, "E124.0.4", {"start": v(-34.29, 6.4) * mm, "end": v(-40.64, 6.4) * mm});
            skLineSegment(sketch, "E124.0.5", {"start": v(-40.64, 6.4) * mm, "end": v(-40.64, -7.07) * mm});
            skLineSegment(sketch, "E125.0.4", {"start": v(-21.59, 6.4) * mm, "end": v(-27.94, 6.4) * mm});
            skLineSegment(sketch, "E125.0.5", {"start": v(-27.94, 6.4) * mm, "end": v(-27.94, -7.07) * mm});
            skArc(sketch, "E126.0.0", {"start": v(-15.24, -7.07) * mm, "mid": v(-11.85, -16.66) * mm, "end": v(-3.18, -21.98) * mm});
            skArc(sketch, "E126.0.2", {"start": v(3.18, -15.38) * mm, "mid": v(-5.04, -14.4) * mm, "end": v(-8.9, -7.07) * mm});
            skLineSegment(sketch, "E126.0.3", {"start": v(-8.9, -7.07) * mm, "end": v(-8.9, 6.4) * mm});
            skLineSegment(sketch, "E126.0.4", {"start": v(-8.9, 6.4) * mm, "end": v(-15.24, 6.4) * mm});
            skLineSegment(sketch, "E126.0.5", {"start": v(-15.24, 6.4) * mm, "end": v(-15.24, -7.07) * mm});
            skArc(sketch, "E127.0.1", {"start": v(-3.18, -21.98) * mm, "mid": v(9.59, -18.92) * mm, "end": v(15.24, -7.07) * mm});
            skLineSegment(sketch, "E127.0.2", {"start": v(15.24, -7.07) * mm, "end": v(15.24, 6.4) * mm});
            skLineSegment(sketch, "E127.0.3", {"start": v(15.24, 6.4) * mm, "end": v(8.9, 6.4) * mm});
            skLineSegment(sketch, "E127.0.4", {"start": v(8.9, 6.4) * mm, "end": v(8.9, -7.07) * mm});
            skArc(sketch, "E127.0.5", {"start": v(8.9, -7.07) * mm, "mid": v(7.32, -12.11) * mm, "end": v(3.18, -15.38) * mm});
            skArc(sketch, "E128.0.1", {"start": v(-3.18, -34.83) * mm, "mid": v(18.6, -27.92) * mm, "end": v(27.94, -7.07) * mm});
            skLineSegment(sketch, "E128.0.2", {"start": v(27.94, -7.07) * mm, "end": v(27.94, 6.4) * mm});
            skLineSegment(sketch, "E128.0.3", {"start": v(27.94, 6.4) * mm, "end": v(21.59, 6.4) * mm});
            skLineSegment(sketch, "E128.0.4", {"start": v(21.59, 6.4) * mm, "end": v(21.59, -7.07) * mm});
            skArc(sketch, "E128.0.5", {"start": v(21.59, -7.07) * mm, "mid": v(16.35, -21.17) * mm, "end": v(3.18, -28.43) * mm});
            skArc(sketch, "E129.0.1", {"start": v(-3.18, -47.59) * mm, "mid": v(27.6, -36.91) * mm, "end": v(40.64, -7.07) * mm});
            skLineSegment(sketch, "E129.0.2", {"start": v(40.64, -7.07) * mm, "end": v(40.64, 6.4) * mm});
            skLineSegment(sketch, "E129.0.3", {"start": v(40.64, 6.4) * mm, "end": v(34.29, 6.4) * mm});
            skLineSegment(sketch, "E129.0.4", {"start": v(34.29, 6.4) * mm, "end": v(34.29, -7.07) * mm});
            skArc(sketch, "E129.0.5", {"start": v(34.29, -7.07) * mm, "mid": v(25.34, -30.17) * mm, "end": v(3.18, -41.22) * mm});
            skArc(sketch, "E130.0.1", {"start": v(3.18, -60.32) * mm, "mid": v(38.82, -43.65) * mm, "end": v(53.34, -7.07) * mm});
            skLineSegment(sketch, "E130.0.2", {"start": v(53.34, -7.07) * mm, "end": v(53.34, 6.4) * mm});
            skLineSegment(sketch, "E130.0.3", {"start": v(53.34, 6.4) * mm, "end": v(46.99, 6.4) * mm});
            skLineSegment(sketch, "E130.0.4", {"start": v(46.99, 6.4) * mm, "end": v(46.99, -7.07) * mm});
            skArc(sketch, "E130.0.5", {"start": v(46.99, -7.07) * mm, "mid": v(32.08, -41.4) * mm, "end": v(-3.18, -53.96) * mm});
            skPoint(sketch, "E131.orphan", {"position": v(-3.18, -60.32) * mm});
            skPoint(sketch, "E132.orphan", {"position": v(3.18, -53.96) * mm});
            skPoint(sketch, "E133.orphan", {"position": v(3.18, -47.59) * mm});
            skPoint(sketch, "E134.orphan", {"position": v(-3.18, -41.22) * mm});
            skPoint(sketch, "E135.orphan", {"position": v(3.18, -34.83) * mm});
            skPoint(sketch, "E136.orphan", {"position": v(-3.18, -28.43) * mm});
            skPoint(sketch, "E137.orphan", {"position": v(3.18, -21.98) * mm});
            skPoint(sketch, "E138.orphan", {"position": v(-3.18, -15.38) * mm});
            skLineSegment(sketch, "E139.0", {"start": v(-21.59, -7.07) * mm, "end": v(-21.59, 6.4) * mm});
            skArc(sketch, "E140.0", {"start": v(-21.59, -7.07) * mm, "mid": v(-16.35, -21.17) * mm, "end": v(-3.18, -28.43) * mm});
            skArc(sketch, "E141.0", {"start": v(-27.94, -7.07) * mm, "mid": v(-20.85, -25.67) * mm, "end": v(-3.18, -34.83) * mm});
            skLineSegment(sketch, "E142", {"start": v(-3.18, -28.43) * mm, "end": v(3.18, -28.43) * mm});
            skSolve(sketch);
        }
        {
            var Q0;
            {var subQ0=sQuery(id+"F2.wireOp",EDGE,"E33.trimOffspring");var subQ2=sQuery(id+"F5.wireOp",EDGE,"E72");var subQ5=makeQuery(id+"F5.imprint","INTERSECT",VERTEX,{"derivedFrom":[makeQuery(id+"F3.boolean.opBoolean","COPY",EDGE,{"derivedFrom":makeQuery(id+"F3.opExtrude","CAP_EDGE",EDGE,{"disambiguationData":[OSD([subQ0])],"isStart":false})}),subQ2]});Q0=makeQuery(id+"F5.imprint","IMPRINT",FACE,{"disambiguationData":[TD([[makeQuery(id+"F5.imprint","IMPRINT",EDGE,{"disambiguationData":[TD([[subQ5,1.0]])],"derivedFrom":subQ2}),1.0]])]});}
            var Q1;
            Q1=qSketchRegion(id+"F13",true);
            var Q2;
            Q2=sQuery(id+"F24.wireOp",EDGE,"E123.0.5");
            var Q3;
            Q3=sQuery(id+"F24.wireOp",EDGE,"E123.0.0");
            var Q4;
            Q4=sQuery(id+"F24.wireOp",EDGE,"E130.0.1");
            var Q5;
            Q5=sQuery(id+"F24.wireOp",EDGE,"E130.0.2");
            sweep(context, id + "F25", {"operationType" : NewBodyOperationType.REMOVE, "profiles" : qUnion([Q0, Q1]), "path" : qUnion([Q2, Q3, Q4, Q5])});
        }
        {
            var Q0;
            {var subQ0=sQuery(id+"F2.wireOp",EDGE,"E32.trimOffspring");var subQ2=sQuery(id+"F5.wireOp",EDGE,"E64");var subQ5=makeQuery(id+"F5.imprint","INTERSECT",VERTEX,{"derivedFrom":[makeQuery(id+"F3.boolean.opBoolean","COPY",EDGE,{"derivedFrom":makeQuery(id+"F3.opExtrude","CAP_EDGE",EDGE,{"disambiguationData":[OSD([subQ0])],"isStart":false})}),subQ2]});Q0=makeQuery(id+"F5.imprint","IMPRINT",FACE,{"disambiguationData":[TD([[makeQuery(id+"F5.imprint","IMPRINT",EDGE,{"disambiguationData":[TD([[subQ5,1.0]])],"derivedFrom":subQ2}),1.0]])]});}
            var Q1;
            Q1=sQuery(id+"F24.wireOp",EDGE,"E124.0.5");
            var Q2;
            Q2=sQuery(id+"F24.wireOp",EDGE,"E124.0.0");
            var Q3;
            Q3=sQuery(id+"F24.wireOp",EDGE,"E129.0.1");
            var Q4;
            Q4=sQuery(id+"F24.wireOp",EDGE,"E129.0.2");
            sweep(context, id + "F26", {"operationType" : NewBodyOperationType.REMOVE, "profiles" : qUnion([Q0]), "path" : qUnion([Q1, Q2, Q3, Q4])});
        }
        {
            var Q0;
            {var subQ0=sQuery(id+"F2.wireOp",EDGE,"E31.trimOffspring");var subQ2=sQuery(id+"F5.wireOp",EDGE,"E65");var subQ5=makeQuery(id+"F5.imprint","INTERSECT",VERTEX,{"derivedFrom":[makeQuery(id+"F3.boolean.opBoolean","COPY",EDGE,{"derivedFrom":makeQuery(id+"F3.opExtrude","CAP_EDGE",EDGE,{"disambiguationData":[OSD([subQ0])],"isStart":false})}),subQ2]});Q0=makeQuery(id+"F5.imprint","IMPRINT",FACE,{"disambiguationData":[TD([[makeQuery(id+"F5.imprint","IMPRINT",EDGE,{"disambiguationData":[TD([[subQ5,1.0]])],"derivedFrom":subQ2}),1.0]])]});}
            var Q1;
            Q1=sQuery(id+"F24.wireOp",EDGE,"E125.0.5");
            var Q2;
            Q2=makeQuery(id+"F18.opExtrude","CAP_EDGE",EDGE,{"disambiguationData":[OSD([sQuery(id+"F2.wireOp",EDGE,"E7.0")])],"isStart":false});
            var Q3;
            Q3=sQuery(id+"F24.wireOp",EDGE,"E128.0.1");
            var Q4;
            Q4=sQuery(id+"F24.wireOp",EDGE,"E128.0.2");
            sweep(context, id + "F27", {"operationType" : NewBodyOperationType.REMOVE, "profiles" : qUnion([Q0]), "path" : qUnion([Q1, Q2, Q3, Q4])});
        }
        {
            var Q0;
            {var subQ0=sQuery(id+"F2.wireOp",EDGE,"E34");var subQ2=sQuery(id+"F5.wireOp",EDGE,"E66");var subQ5=makeQuery(id+"F5.imprint","INTERSECT",VERTEX,{"derivedFrom":[makeQuery(id+"F3.boolean.opBoolean","COPY",EDGE,{"derivedFrom":makeQuery(id+"F3.opExtrude","CAP_EDGE",EDGE,{"disambiguationData":[OSD([subQ0])],"isStart":false})}),subQ2]});Q0=makeQuery(id+"F5.imprint","IMPRINT",FACE,{"disambiguationData":[TD([[makeQuery(id+"F5.imprint","IMPRINT",EDGE,{"disambiguationData":[TD([[subQ5,1.0]])],"derivedFrom":subQ2}),1.0]])]});}
            var Q1;
            Q1=sQuery(id+"F5.wireOp",EDGE,"E66");
            var Q2;
            Q2=sQuery(id+"F24.wireOp",EDGE,"E126.0.5");
            var Q3;
            Q3=sQuery(id+"F24.wireOp",EDGE,"E126.0.0");
            var Q4;
            Q4=sQuery(id+"F24.wireOp",EDGE,"E127.0.1");
            var Q5;
            Q5=sQuery(id+"F24.wireOp",EDGE,"E127.0.2");
            sweep(context, id + "F28", {"operationType" : NewBodyOperationType.REMOVE, "profiles" : qUnion([Q0]), "surfaceProfiles" : qUnion([Q1]), "path" : qUnion([Q2, Q3, Q4, Q5])});
        }
        {
            var Q0;
            {var subQ77=sQuery(id+"F0.wireOp",EDGE,"E1");Q0=makeQuery(id+"F5.imprint","IMPRINT",FACE,{"disambiguationData":[TD([[makeQuery(id+"F5.imprint","IMPRINT",EDGE,{"derivedFrom":makeQuery(id+"F1.opExtrude","CAP_EDGE",EDGE,{"disambiguationData":[OSD([subQ77])],"isStart":false})}),1.0]])]});}
            cPlane(context, id + "F29", {"entities" : qUnion([Q0]), "cplaneType" : CPlaneType.OFFSET, "offset" : 0 * mm, "width" : 152.4 * mm, "height" : 152.4 * mm});
        }
        {
            var Q0;
            {var subQ0=sQuery(id+"F0.wireOp",EDGE,"E0");var subQ1=sQuery(id+"F0.wireOp",EDGE,"E1");Q0=makeQuery(id+"F3.boolean.opBoolean","SPLIT",FACE,{"disambiguationData":[TD([makeQuery(id+"F3.opExtrude","SWEPT_FACE",FACE,{"disambiguationData":[OSD([sQuery(id+"F2.wireOp",EDGE,"E18")])]})])],"derivedFrom":makeQuery(id+"F1.opExtrude","CAP_FACE",FACE,{"disambiguationData":[OSD([subQ0,subQ1])],"isStart":true})});}
            cPlane(context, id + "F30", {"entities" : qUnion([Q0]), "cplaneType" : CPlaneType.OFFSET, "offset" : 0 * mm, "width" : 152.4 * mm, "height" : 152.4 * mm});
        }
        {
            var Q0;
            Q0=qCreatedBy(id+"F30.planeOp",FACE);
            var sketch = newSketch(context, id + "F31", { "sketchPlane" : qUnion([Q0])});
            skArc(sketch, "E143.0", {"start": v(66.37, 6.4) * mm, "mid": v(50.4, -43.64) * mm, "end": v(3.17, -66.6) * mm});
            skArc(sketch, "E144.0", {"start": v(3.17, -66.6) * mm, "mid": v(0, -66.68) * mm, "end": v(-3.17, -66.6) * mm});
            skArc(sketch, "E145.0", {"start": v(-3.18, -66.6) * mm, "mid": v(-50.4, -43.64) * mm, "end": v(-66.37, 6.4) * mm});
            skLineSegment(sketch, "E146", {"start": v(-66.37, 6.4) * mm, "end": v(66.37, 6.4) * mm});
            skSolve(sketch);
        }
        {
            var Q0;
            Q0 = qSketchRegion(id + "F31", true);
            extrude(context, id + "F32", {"entities" : qUnion([Q0]), "operationType" : NewBodyOperationType.ADD, "depth" : 3.17 * mm});
        }
        {
            var Q0;
            {var subQ0=sQuery(id+"F0.wireOp",EDGE,"E1");Q0=makeQuery(id+"F5.imprint","IMPRINT",FACE,{"disambiguationData":[TD([[makeQuery(id+"F5.imprint","IMPRINT",EDGE,{"derivedFrom":makeQuery(id+"F1.opExtrude","CAP_EDGE",EDGE,{"disambiguationData":[OSD([subQ0])],"isStart":false})}),1.0]])]});}
            var sketch = newSketch(context, id + "F33", { "sketchPlane" : qUnion([Q0])});
            skPoint(sketch, "E147.0", {"position": v(-50.12, -6.35) * mm});
            skCircle(sketch, "E148", {"center": v(-50.12, -6.35) * mm, "radius": 3.12 * mm});
            skSolve(sketch);
        }
        {
            var Q0;
            {var subQ0=sQuery(id+"F0.wireOp",EDGE,"E1");Q0=makeQuery(id+"F5.imprint","IMPRINT",FACE,{"disambiguationData":[TD([[makeQuery(id+"F5.imprint","IMPRINT",EDGE,{"derivedFrom":makeQuery(id+"F1.opExtrude","CAP_EDGE",EDGE,{"disambiguationData":[OSD([subQ0])],"isStart":false})}),1.0]])]});}
            var sketch = newSketch(context, id + "F34", { "sketchPlane" : qUnion([Q0])});
            skCircle(sketch, "E149.0", {"center": v(-50.12, -6.35) * mm, "radius": 4.76 * mm});
            skCircle(sketch, "E150.0", {"center": v(-50.12, -6.35) * mm, "radius": 6.03 * mm});
            skSolve(sketch);
        }
        {
            var Q0;
            Q0 = qSketchRegion(id + "F33", true);
            extrude(context, id + "F35", {"entities" : qUnion([Q0]), "depth" : 6.35 * mm, "hasSecondDirection" : true, "secondDirectionOppositeDirection" : true, "secondDirectionDepth" : 12.7 * mm});
        }
        {
            var Q0;
            Q0 = qSketchRegion(id + "F34", true);
            extrude(context, id + "F36", {"entities" : qUnion([Q0]), "operationType" : NewBodyOperationType.ADD, "depth" : 12.7 * mm});
        }
        {
            var Q0;
            Q0=makeQuery(id+"F35.opExtrude","CAP_FACE",FACE,{"disambiguationData":[OSD([sQuery(id+"F33.wireOp",EDGE,"E148")])],"isStart":false});
            var sketch = newSketch(context, id + "F37", { "sketchPlane" : qUnion([Q0])});
            skCircle(sketch, "E151.0", {"center": v(-50.12, -6.35) * mm, "radius": 4.76 * mm});
            skSolve(sketch);
        }
        {
            var Q0;
            Q0 = qSketchRegion(id + "F37", true);
            var Q1;
            Q1=makeQuery(id+"F1.opExtrude","SWEPT_FACE",FACE,{"disambiguationData":[OSD([sQuery(id+"F0.wireOp",EDGE,"E1")])]});
            var Q2;
            Q2=makeQuery(id+"F1.opExtrude","SWEPT_BODY",BODY,{"disambiguationData":[OSD([sQuery(id+"F0.wireOp",EDGE,"E0"),sQuery(id+"F0.wireOp",EDGE,"E1")])]});
            extrude(context, id + "F38", {"entities" : qUnion([Q0]), "operationType" : NewBodyOperationType.ADD, "endBound" : BoundingType.UP_TO_SURFACE, "oppositeDirection" : true, "endBoundEntityFace" : qUnion([Q1]), "endBoundEntityBody" : qUnion([Q2]), "depth" : 25.4 * mm});
        }
        {
            var Q0;
            Q0=qCreatedBy(id+"F4.planeOp",FACE);
            var sketch = newSketch(context, id + "F39", { "sketchPlane" : qUnion([Q0])});
            skPoint(sketch, "E152.0", {"position": v(50.12, 6.4) * mm});
            skLineSegment(sketch, "E153", {"start": v(45.36, 31.8) * mm, "end": v(43.81, 31.8) * mm});
            skPoint(sketch, "E154.0", {"position": v(46.99, 6.4) * mm});
            skLineSegment(sketch, "E155", {"start": v(46.99, 6.4) * mm, "end": v(43.81, 31.8) * mm});
            skLineSegment(sketch, "E156", {"start": v(46.99, 6.4) * mm, "end": v(46.99, -4) * mm});
            skLineSegment(sketch, "E157.top", {"start": v(50.12, 25.45) * mm, "end": v(45.36, 25.45) * mm});
            skLineSegment(sketch, "E157.right", {"start": v(45.36, 31.8) * mm, "end": v(45.36, 25.45) * mm});
            skPoint(sketch, "E158.0", {"position": v(40.64, 6.4) * mm});
            skLineSegment(sketch, "E159", {"start": v(50.12, 25.45) * mm, "end": v(50.12, -4) * mm});
            skLineSegment(sketch, "E160", {"start": v(46.99, -4) * mm, "end": v(50.12, -4) * mm});
            skSolve(sketch);
        }
        {
            var Q0;
            Q0=qCreatedBy(id+"F4.planeOp",FACE);
            var sketch = newSketch(context, id + "F40", { "sketchPlane" : qUnion([Q0])});
            skLineSegment(sketch, "E161.0", {"start": v(50.12, 25.45) * mm, "end": v(50.12, -4) * mm});
            skSolve(sketch);
        }
        {
            var Q0;
            Q0=makeQuery(id+"F39.imprint","IMPRINT",FACE,{"disambiguationData":[TD([[makeQuery(id+"F39.imprint","IMPRINT",EDGE,{"derivedFrom":sQuery(id+"F39.wireOp",EDGE,"E153")}),1.0]])]});
            var Q1;
            Q1=sQuery(id+"F40.wireOp",EDGE,"E161.0");
            revolve(context, id + "F41", {"entities" : qUnion([Q0]), "axis" : qUnion([Q1]), "revolveType" : RevolveType.FULL});
        }
    });
